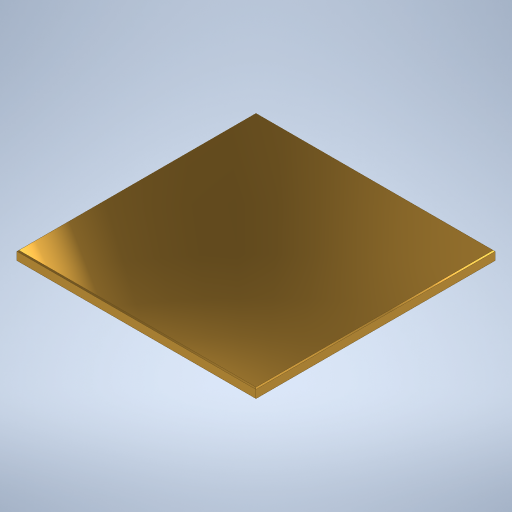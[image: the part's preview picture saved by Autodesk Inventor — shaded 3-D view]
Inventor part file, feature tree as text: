
AUTODESK INVENTOR PART (.ipt)
format: ipt  version: 2023 (Build 270158000, 158)  size: 257,536 bytes
history: native  units: mm
features: other x1, extrude x1, chamfer x1, sketch x1
ambient origin geometry x8: Origin, YZ Plane, XZ Plane, XY Plane, X Axis, Y Axis, Z Axis, Center Point
bodies: Body1 (feature_tree)
feature tree (4):
  other  "Sólido1"
  extrude  "Extrusão1"  Depth=120.0mm
  chamfer  "Chamfer1"  Distance=5.0mm
  sketch  "Esboço1"  dims[d0=120.0mm d1=120.0mm d2=5.0mm d3=0.0mm d4=0.5mm d5=2.0mm d6=45.0deg]
